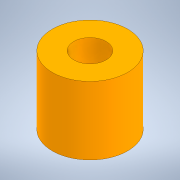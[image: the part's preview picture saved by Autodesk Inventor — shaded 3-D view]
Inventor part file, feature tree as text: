
AUTODESK INVENTOR PART (.ipt)
format: ipt  version: 2020 (Build 240168000, 168)  size: 100,864 bytes
history: native  units: mm
features: extrude x1, sketch x1
ambient origin geometry x8: Origin, YZ Plane, XZ Plane, XY Plane, X Axis, Y Axis, Z Axis, Center Point
bodies: Solid1 (feature_tree)
feature tree (2):
  extrude  "Extrusion1"  Depth=6.33mm
  sketch  "Sketch1"  dims[d0=3.0mm d1=7.0mm d2=6.33mm d3=0.0mm]
